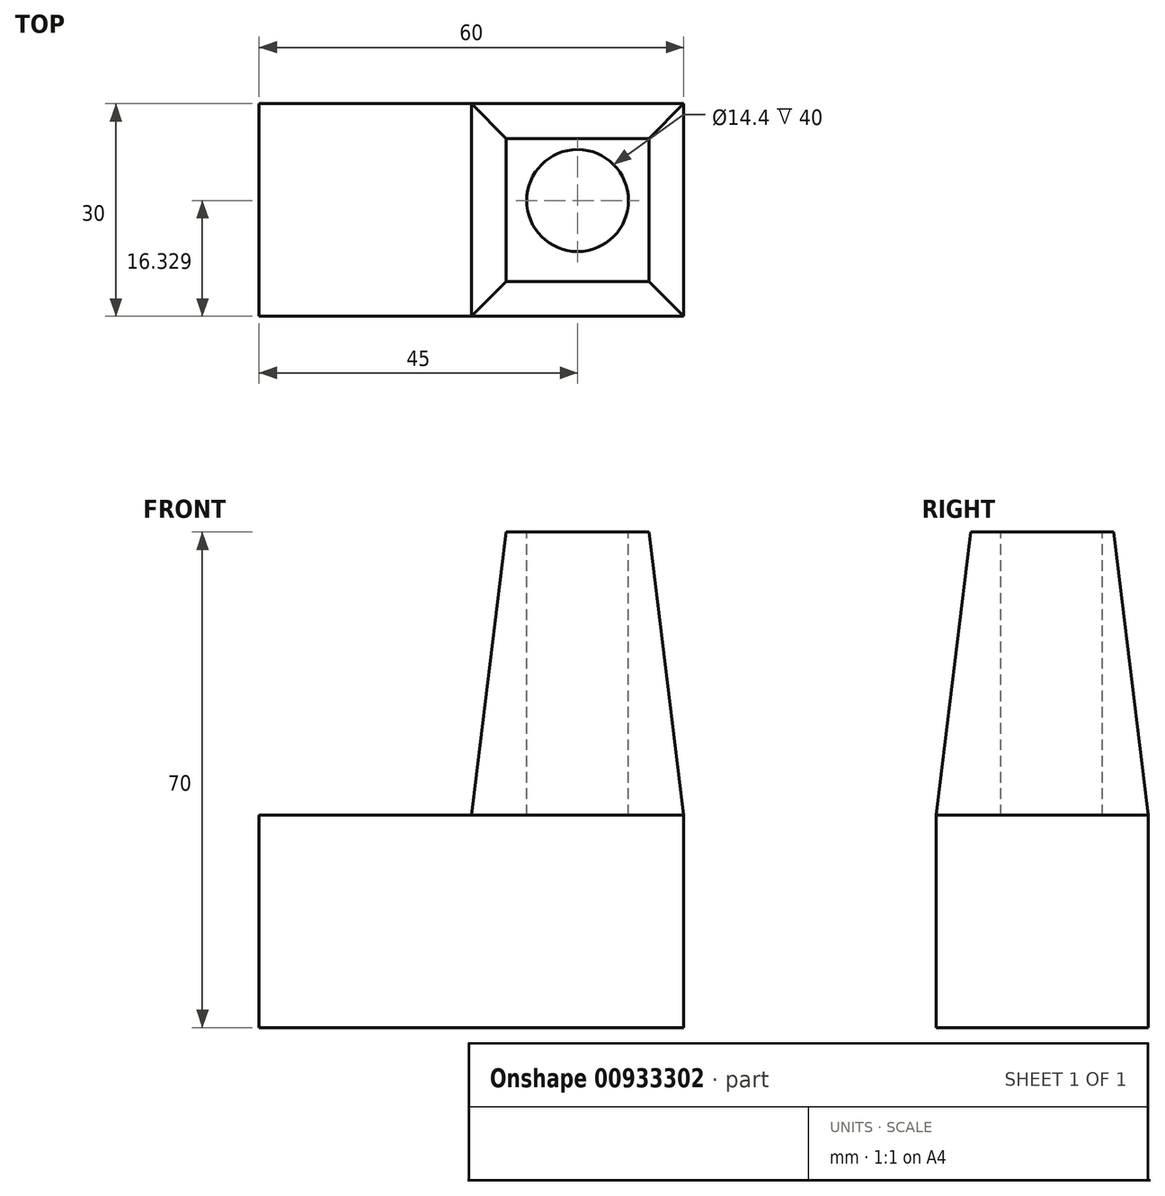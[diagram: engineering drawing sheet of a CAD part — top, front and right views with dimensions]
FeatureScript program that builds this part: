
annotation { "Feature Type Name" : "Feature", "Feature Type Description" : "" }
export const myFeature = defineFeature(function(context is Context, id is Id, definition is map)
    precondition{}
    {
        {
            var Q0;
            Q0=qCreatedBy(makeId("Front.planeOp"),FACE);
            var sketch = newSketch(context, id + "F0", { "sketchPlane" : qUnion([Q0])});
            skLineSegment(sketch, "E0.bottom", {"start": v(-60, 0) * mm, "end": v(0, 0) * mm});
            skLineSegment(sketch, "E0.top", {"start": v(-60, -30) * mm, "end": v(0, -30) * mm});
            skLineSegment(sketch, "E0.left", {"start": v(-60, 0) * mm, "end": v(-60, -30) * mm});
            skLineSegment(sketch, "E0.right", {"start": v(0, 0) * mm, "end": v(0, -30) * mm});
            skSolve(sketch);
        }
        {
            var Q0;
            Q0=makeQuery(id+"F0.imprint","IMPRINT",FACE,{"disambiguationData":[TD([[makeQuery(id+"F0.imprint","IMPRINT",EDGE,{"derivedFrom":sQuery(id+"F0.wireOp",EDGE,"E0.bottom")}),-1.0]])]});
            extrude(context, id + "F1", {"entities" : qUnion([Q0]), "depth" : 30 * mm, "offsetDistance" : 25.4 * mm});
        }
        {
            var Q0;
            Q0=makeQuery(id+"F1.opExtrude","SWEPT_FACE",FACE,{"disambiguationData":[OSD([sQuery(id+"F0.wireOp",EDGE,"E0.bottom")])]});
            var sketch = newSketch(context, id + "F2", { "sketchPlane" : qUnion([Q0])});
            skLineSegment(sketch, "E1.bottom", {"start": v(0, 0) * mm, "end": v(-30, 0) * mm});
            skLineSegment(sketch, "E1.top", {"start": v(0, -30) * mm, "end": v(-30, -30) * mm});
            skLineSegment(sketch, "E1.left", {"start": v(0, 0) * mm, "end": v(0, -30) * mm});
            skLineSegment(sketch, "E1.right", {"start": v(-30, 0) * mm, "end": v(-30, -30) * mm});
            skSolve(sketch);
        }
        {
            var Q0;
            Q0=makeQuery(id+"F2.imprint","IMPRINT",FACE,{"disambiguationData":[TD([[makeQuery(id+"F2.imprint","IMPRINT",EDGE,{"derivedFrom":sQuery(id+"F2.wireOp",EDGE,"E1.bottom")}),-1.0]])]});
            extrude(context, id + "F3", {"entities" : qUnion([Q0]), "operationType" : NewBodyOperationType.ADD, "depth" : 40 * mm, "offsetDistance" : 25.4 * mm, "hasDraft" : true, "draftAngle" : 7 * degree, "draftPullDirection" : true});
        }
        {
            var Q0;
            Q0=makeQuery(id+"F3.opExtrude","CAP_FACE",FACE,{"disambiguationData":[OSD([sQuery(id+"F2.wireOp",EDGE,"E1.bottom"),sQuery(id+"F2.wireOp",EDGE,"E1.top"),sQuery(id+"F2.wireOp",EDGE,"E1.left"),sQuery(id+"F2.wireOp",EDGE,"E1.right")])],"isStart":false});
            var sketch = newSketch(context, id + "F4", { "sketchPlane" : qUnion([Q0])});
            skCircle(sketch, "E2", {"center": v(-15, -13.67) * mm, "radius": 7.2 * mm});
            skPoint(sketch, "E2.centerSnap0", {"position": v(-15, -25.09) * mm});
            skSolve(sketch);
        }
        {
            var Q0;
            Q0=makeQuery(id+"F4.imprint","IMPRINT",FACE,{"disambiguationData":[TD([[makeQuery(id+"F4.imprint","IMPRINT",EDGE,{"derivedFrom":sQuery(id+"F4.wireOp",EDGE,"E2")}),1.0]])]});
            extrude(context, id + "F5", {"entities" : qUnion([Q0]), "operationType" : NewBodyOperationType.REMOVE, "oppositeDirection" : true, "depth" : 40 * mm, "offsetDistance" : 25.4 * mm});
        }
    });
